# Revit family: DUPLEXVENT Flexi DV1100
name_source: partatom
category: Mechanical Equipment
revit_build: Autodesk Revit 2015 (Build: 20140606_1530(x64)
units: mm (PartAtom-declared; Revit-internal decimal feet)

## types (1)
- FLEXI DV1100
    100% Summer/Winter by-pass = Yes
    Air Volume @ Pa = 1000@200Pa
    Airflow Developments Limited = Lancaster Road,Cressex Business Park ,HighWycombe ,HP12 3QP
Cressex Business Park,
HighWycombe,HP12 3QP
HighWycombe,HP12 3QP
    Balanced supply and extract air ventilation with heat recovery = Yes
    Carbon dioxide control (optional) = Yes
    Condensate pipe dia = 21mm
    Control Optional = Humidity , CO2 , Air quality
    Control Standard = Digital - 10 Speed , BMS (MODBUS) + Internet
    Depth mm = 395
    Duct Connections = 4 x 250mm dia
    EC motor for fine speed control = Yes
    Electronic control panel with LCD display = Yes
    Excellent heat recovery efficiency of the counter flow cell = Yes
    Extract air filter = M5
    Fan input = 93-385 W DC
    Filter maintenance reminder = Yes
    Frequency = 50Hz
    Frost protection = Included
    Heat Exchanger = Counterflow
    Heat Recovery = >90%
    Height mm = 1100
    Humidity control (optional) = Yes
    Internet connection = Yes
    Max Air Volume  m3/hr = 1200
    Meets Building Regulations Approved Document F 2010 = Yes
    Model = FLEXI DV1100
    Part number = 90000183
    Passive House Certified = Yes
    Post-heater = Optional  3000 W
    Pre-heater = Optional  3000 W
    SAP Appendix Q Eligible = No
    Summer By-pass = Automatic
    Supply air filter = F7
    Technical support = 01494 560950
    Telephone = 01494 525252
    Versatile positioning (floor/ceiling installation) = Yes
    Voltage Supply      Single Phase = 220-240v ac
    Warranty = 3 Years
    Water or DX heating and cooling coils (optional) = Yes
    Web site = www.airflow.com
    Weekly clock control as a standard feature = Yes
    Width mm = 1700

## geometry (parser evidence)
native form markers: Blend x6, Sweep x2
no freeform markers — native parametric forms only
